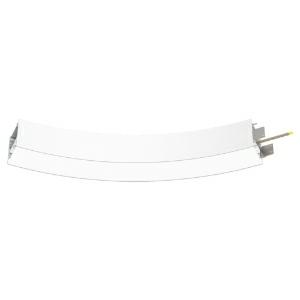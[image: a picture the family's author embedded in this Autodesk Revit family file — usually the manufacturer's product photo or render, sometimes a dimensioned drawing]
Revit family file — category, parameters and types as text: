
# Revit family: super-g_slim_super_g_slim_1550_45deg_hl_ps_led__12w_1580lm_3000k_cri_80_430-1660_ec51
name_source: partatom
category: Leuchten
revit_build: Autodesk Revit 2016 (Build: 20190508_0715(x64)
units: mm (PartAtom-declared; Revit-internal decimal feet)

## family parameters
Basisbauteil = Fläche
Beim Laden mit Abzugskörper schneiden = Nein
Bemaßung runder Anschluss = Durchmesser verwenden
Gemeinsam genutzt = Nein
Lichtquelle = Nein
Raumberechnungspunkt = Nein
Teiletyp = Normal

## types (1)
- 430-1660-D01 (1 x LED, 480 lm, 3000K)
    Approval mark = CE
    Beschreibung = The insert consists of aluminum-extruded profile. Charming SOFT-EDGE design ensure unparalleled styling. The ballast is integrated and allows for an operation with 220-240V (50/60Hz). SUPER-G SLIM (# 430-1660) ist not dimmable (on/off).
    CIE Flux Codes = 48 79 96 100 71
    Color Rendering = 1B/80…89
    Color Temperature = 3000K
    Height = 90 mm
    Hersteller = Prolicht
    Lamp Light Flux = 480 lm
    Lamp count = 1
    Lampe = 1 x LED
    Length = 146 mm
    Luminous efficacy = 103 lm/W
    ModVariant = Nein
    Modell = 430-1660
    Mounting Place = Ceiling
    Mounting Type = Pendant
    Number of Poles = 1
    OnlyDefault = Ja
    Power Factor = 1
    Product Name = SUPER-G SLIM__SUPER G SLIM 1550/45° HL PS LED: 12W 1580lm 3000K CRI:80
    Product group = Suspended profile systems
    ProductGroupID = 944
    Protection Class = Protection class I
    Protection Degree = IP 20
    RLX_Detail_Level = 1
    RlxData = <blob elided: 33849 chars, md5=ac06fb86>
    Scheinlast = 13 VA
    Socket = socket
    Standby Power = 0 W
    System Light Flux = 1361 lm
    System Power = 13 W
    Typenbild = 430-1660.jpg
    URL = http://relux.com
    VarID = 430-1660-d01
    Voltage = 0 V
    Vorgabe-Ansicht = 1800 mm
    Weight = 0.00 kg
    Width = 65 mm

## geometry (parser evidence)
native form markers: Blend x4, Sweep x19
no freeform markers — native parametric forms only
